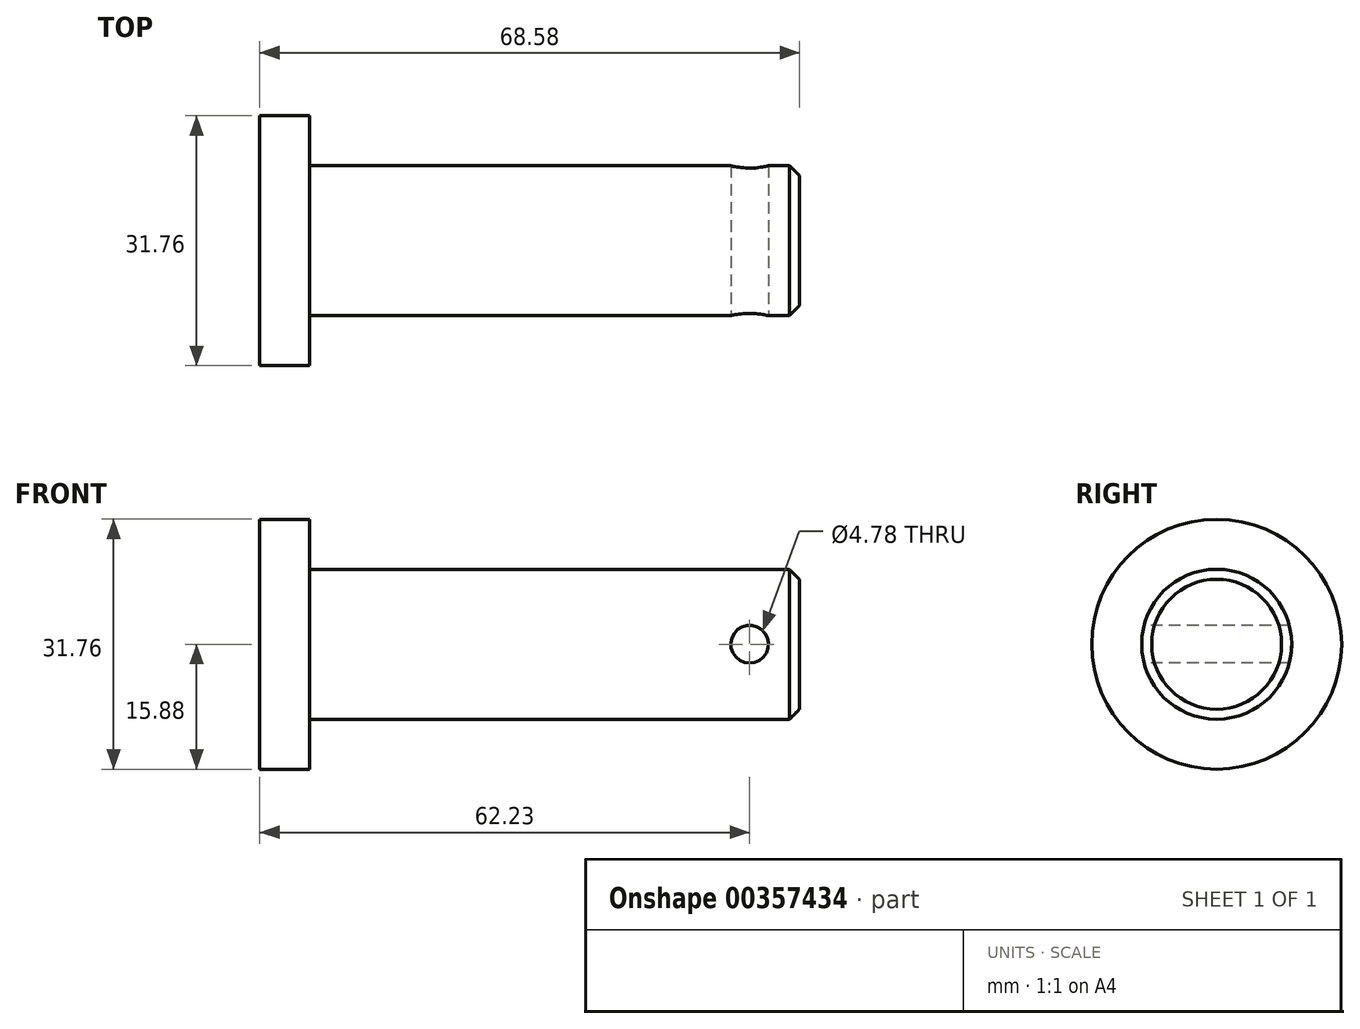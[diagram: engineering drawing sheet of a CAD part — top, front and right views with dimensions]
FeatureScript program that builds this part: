
annotation { "Feature Type Name" : "Feature", "Feature Type Description" : "" }
export const myFeature = defineFeature(function(context is Context, id is Id, definition is map)
    precondition{}
    {
        {
            var Q0;
            Q0=qCreatedBy(makeId("Right.planeOp"),FACE);
            var sketch = newSketch(context, id + "F0", { "sketchPlane" : qUnion([Q0])});
            skCircle(sketch, "E0", {"center": v(0, 0) * mm, "radius": 15.88 * mm});
            skSolve(sketch);
        }
        {
            var Q0;
            Q0=makeQuery(id+"F0.imprint","IMPRINT",FACE,{"disambiguationData":[TD([[makeQuery(id+"F0.imprint","IMPRINT",EDGE,{"derivedFrom":sQuery(id+"F0.wireOp",EDGE,"E0")}),1.0]])]});
            extrude(context, id + "F1", {"entities" : qUnion([Q0]), "depth" : 6.35 * mm});
        }
        {
            var Q0;
            Q0=makeQuery(id+"F1.opExtrude","CAP_FACE",FACE,{"disambiguationData":[OSD([sQuery(id+"F0.wireOp",EDGE,"E0")])],"isStart":false});
            var sketch = newSketch(context, id + "F2", { "sketchPlane" : qUnion([Q0])});
            skCircle(sketch, "E1", {"center": v(0, 0) * mm, "radius": 9.53 * mm});
            skSolve(sketch);
        }
        {
            var Q0;
            Q0=makeQuery(id+"F2.imprint","IMPRINT",FACE,{"disambiguationData":[TD([[makeQuery(id+"F2.imprint","IMPRINT",EDGE,{"derivedFrom":sQuery(id+"F2.wireOp",EDGE,"E1")}),1.0]])]});
            extrude(context, id + "F3", {"entities" : qUnion([Q0]), "operationType" : NewBodyOperationType.ADD, "depth" : 62.23 * mm});
        }
        {
            var Q0;
            Q0=qCreatedBy(makeId("Front.planeOp"),FACE);
            var sketch = newSketch(context, id + "F4", { "sketchPlane" : qUnion([Q0])});
            skLineSegment(sketch, "E2", {"start": v(0, 0) * mm, "end": v(58.64, 0) * mm, "construction": true});
            skCircle(sketch, "E3", {"center": v(62.23, 0) * mm, "radius": 2.39 * mm});
            skSolve(sketch);
        }
        {
            var Q0;
            Q0 = qSketchRegion(id + "F4", true);
            extrude(context, id + "F5", {"entities" : qUnion([Q0]), "operationType" : NewBodyOperationType.REMOVE, "endBound" : BoundingType.SYMMETRIC, "oppositeDirection" : true, "depth" : 25.4 * mm});
        }
        {
            var Q0;
            Q0=makeQuery(id+"F3.opExtrude","CAP_EDGE",EDGE,{"disambiguationData":[OSD([sQuery(id+"F2.wireOp",EDGE,"E1")])],"isStart":false});
            chamfer(context, id + "F6", {"entities" : qUnion([Q0]), "chamferType" : ChamferType.OFFSET_ANGLE, "width" : 1.27 * mm, "oppositeDirection" : false, "angle" : 45 * degree, "tangentPropagation" : true});
        }
    });
